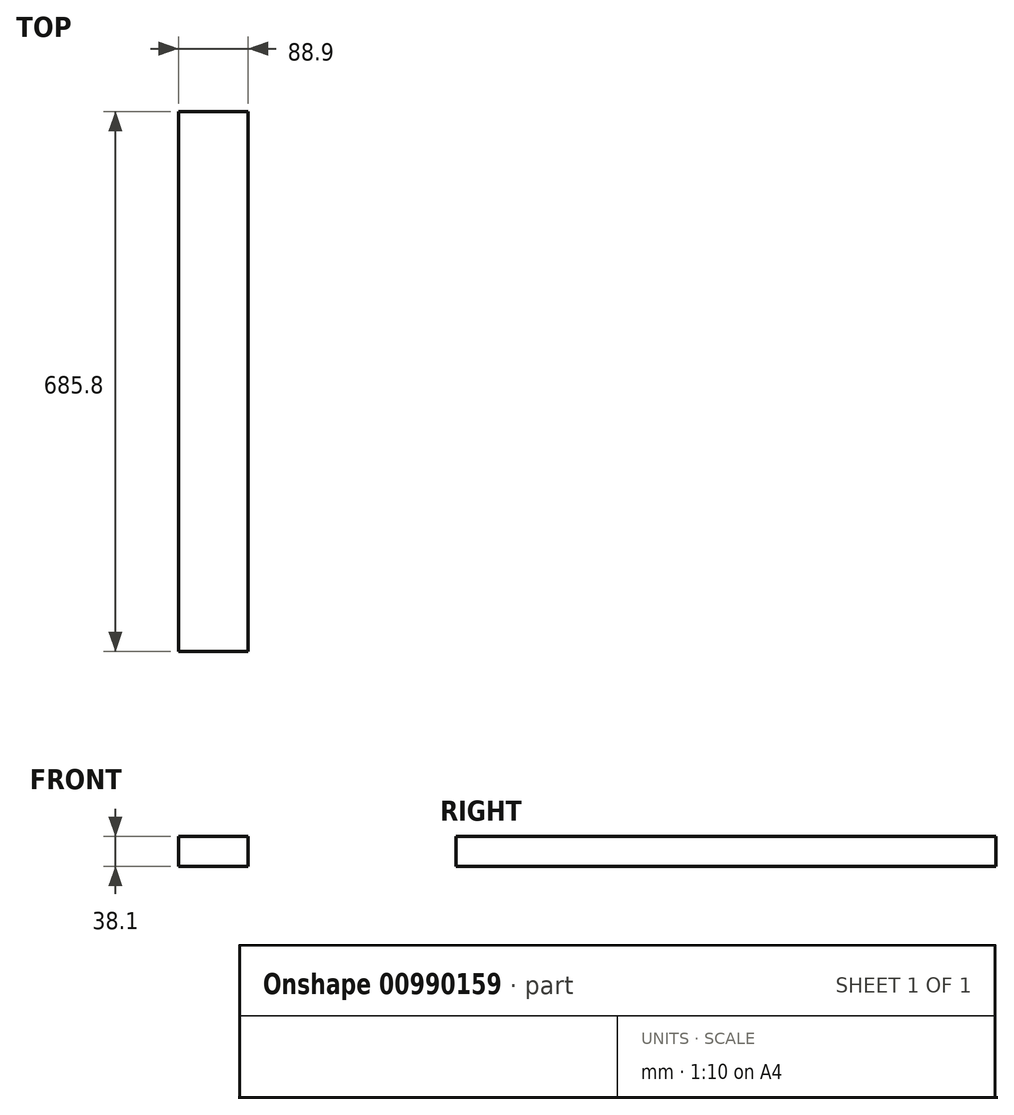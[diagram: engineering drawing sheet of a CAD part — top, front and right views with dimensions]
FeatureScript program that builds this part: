
annotation { "Feature Type Name" : "Feature", "Feature Type Description" : "" }
export const myFeature = defineFeature(function(context is Context, id is Id, definition is map)
    precondition{}
    {
        {
            assignVariable(context, id + "F0", {"name" : "w", "anyValue" : 38.1 * mm});
        }
        {
            var Q0;
            Q0=qCreatedBy(makeId("Top.planeOp"),FACE);
            var sketch = newSketch(context, id + "F1", { "sketchPlane" : qUnion([Q0])});
            skLineSegment(sketch, "E0.bottom", {"start": v(44.45, 342.9) * mm, "end": v(-44.45, 342.9) * mm});
            skLineSegment(sketch, "E0.top", {"start": v(44.45, -342.9) * mm, "end": v(-44.45, -342.9) * mm});
            skLineSegment(sketch, "E0.left", {"start": v(44.45, 342.9) * mm, "end": v(44.45, -342.9) * mm});
            skLineSegment(sketch, "E0.right", {"start": v(-44.45, 342.9) * mm, "end": v(-44.45, -342.9) * mm});
            skPoint(sketch, "E0.middle", {"position": v(0, 0) * mm});
            skSolve(sketch);
        }
        {
            var Q0;
            Q0=qSketchRegion(id+"F1",true);
            extrude(context, id + "F2", {"entities" : qUnion([Q0]), "depth" : getVariable(context, 'w'), "offsetDistance" : 25.4 * mm});
        }
    });
